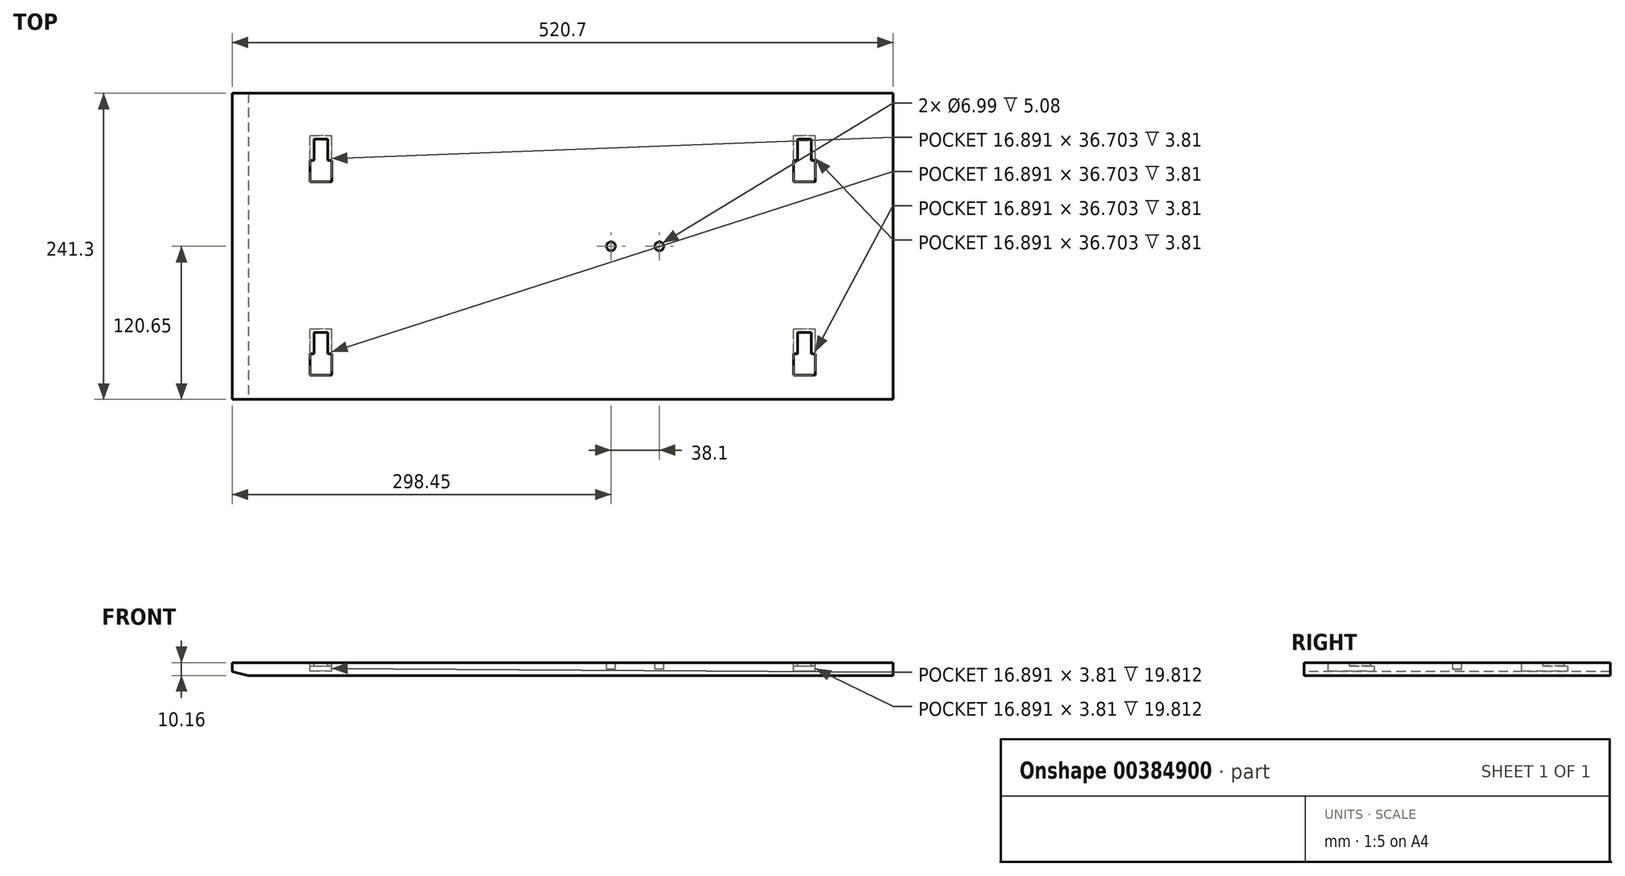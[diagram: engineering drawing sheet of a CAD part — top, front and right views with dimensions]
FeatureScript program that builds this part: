
annotation { "Feature Type Name" : "Feature", "Feature Type Description" : "" }
export const myFeature = defineFeature(function(context is Context, id is Id, definition is map)
    precondition{}
    {
        {
            var Q0;
            Q0=qCreatedBy(makeId("Top.planeOp"),FACE);
            var sketch = newSketch(context, id + "F0", { "sketchPlane" : qUnion([Q0])});
            skLineSegment(sketch, "E0.bottom", {"start": v(0, 0) * mm, "end": v(520.7, 0) * mm});
            skLineSegment(sketch, "E0.top", {"start": v(0, 241.3) * mm, "end": v(520.7, 241.3) * mm});
            skLineSegment(sketch, "E0.left", {"start": v(0, 0) * mm, "end": v(0, 241.3) * mm});
            skLineSegment(sketch, "E0.right", {"start": v(520.7, 0) * mm, "end": v(520.7, 241.3) * mm});
            skSolve(sketch);
        }
        {
            var Q0;
            Q0=makeQuery(id+"F0.imprint","IMPRINT",FACE,{"disambiguationData":[TD([[makeQuery(id+"F0.imprint","IMPRINT",EDGE,{"derivedFrom":sQuery(id+"F0.wireOp",EDGE,"E0.bottom")}),1.0]])]});
            extrude(context, id + "F1", {"entities" : qUnion([Q0]), "depth" : 10.16 * mm});
        }
        {
            var Q0;
            Q0=makeQuery(id+"F1.opExtrude","CAP_FACE",FACE,{"disambiguationData":[OSD([sQuery(id+"F0.wireOp",EDGE,"E0.bottom"),sQuery(id+"F0.wireOp",EDGE,"E0.top"),sQuery(id+"F0.wireOp",EDGE,"E0.left"),sQuery(id+"F0.wireOp",EDGE,"E0.right")])],"isStart":false});
            var sketch = newSketch(context, id + "F2", { "sketchPlane" : qUnion([Q0])});
            skCircle(sketch, "E1", {"center": v(336.55, 120.65) * mm, "radius": 3.5 * mm});
            skCircle(sketch, "E2", {"center": v(298.45, 120.65) * mm, "radius": 3.5 * mm});
            skSolve(sketch);
        }
        {
            var Q0;
            Q0=makeQuery(id+"F1.opExtrude","CAP_FACE",FACE,{"disambiguationData":[OSD([sQuery(id+"F0.wireOp",EDGE,"E0.bottom"),sQuery(id+"F0.wireOp",EDGE,"E0.top"),sQuery(id+"F0.wireOp",EDGE,"E0.left"),sQuery(id+"F0.wireOp",EDGE,"E0.right")])],"isStart":false});
            var sketch = newSketch(context, id + "F3", { "sketchPlane" : qUnion([Q0])});
            skLineSegment(sketch, "E3.bottom", {"start": v(61.4, 19.05) * mm, "end": v(78.3, 19.05) * mm});
            skLineSegment(sketch, "E3.top", {"start": v(61.4, 55.75) * mm, "end": v(78.3, 55.75) * mm});
            skLineSegment(sketch, "E3.left", {"start": v(61.4, 19.05) * mm, "end": v(61.4, 55.75) * mm});
            skLineSegment(sketch, "E3.right", {"start": v(78.3, 19.05) * mm, "end": v(78.3, 55.75) * mm});
            skLineSegment(sketch, "E4.0.1.0", {"start": v(61.4, 171.45) * mm, "end": v(78.3, 171.45) * mm});
            skLineSegment(sketch, "E4.0.1.1", {"start": v(78.3, 171.45) * mm, "end": v(78.3, 208.15) * mm});
            skLineSegment(sketch, "E4.0.1.2", {"start": v(61.4, 208.15) * mm, "end": v(78.3, 208.15) * mm});
            skLineSegment(sketch, "E4.0.1.3", {"start": v(61.4, 171.45) * mm, "end": v(61.4, 208.15) * mm});
            skLineSegment(sketch, "E4.1.0.0", {"start": v(442.4, 19.05) * mm, "end": v(459.3, 19.05) * mm});
            skLineSegment(sketch, "E4.1.0.1", {"start": v(459.3, 19.05) * mm, "end": v(459.3, 55.75) * mm});
            skLineSegment(sketch, "E4.1.0.2", {"start": v(442.4, 55.75) * mm, "end": v(459.3, 55.75) * mm});
            skLineSegment(sketch, "E4.1.0.3", {"start": v(442.4, 19.05) * mm, "end": v(442.4, 55.75) * mm});
            skLineSegment(sketch, "E4.1.1.0", {"start": v(442.4, 171.45) * mm, "end": v(459.3, 171.45) * mm});
            skLineSegment(sketch, "E4.1.1.1", {"start": v(459.3, 171.45) * mm, "end": v(459.3, 208.15) * mm});
            skLineSegment(sketch, "E4.1.1.2", {"start": v(442.4, 208.15) * mm, "end": v(459.3, 208.15) * mm});
            skLineSegment(sketch, "E4.1.1.3", {"start": v(442.4, 171.45) * mm, "end": v(442.4, 208.15) * mm});
            skLineSegment(sketch, "E4.direction1", {"start": v(61.4, 19.05) * mm, "end": v(442.4, 19.05) * mm, "construction": true});
            skLineSegment(sketch, "E4.direction2", {"start": v(61.4, 19.05) * mm, "end": v(61.4, 171.45) * mm, "construction": true});
            skSolve(sketch);
        }
        {
            var Q0;
            Q0=makeQuery(id+"F3.imprint","IMPRINT",FACE,{"disambiguationData":[TD([[makeQuery(id+"F3.imprint","IMPRINT",EDGE,{"derivedFrom":sQuery(id+"F3.wireOp",EDGE,"E4.0.1.0")}),1.0]])]});
            var Q1;
            Q1=makeQuery(id+"F3.imprint","IMPRINT",FACE,{"disambiguationData":[TD([[makeQuery(id+"F3.imprint","IMPRINT",EDGE,{"derivedFrom":sQuery(id+"F3.wireOp",EDGE,"E3.bottom")}),1.0]])]});
            var Q2;
            Q2=makeQuery(id+"F3.imprint","IMPRINT",FACE,{"disambiguationData":[TD([[makeQuery(id+"F3.imprint","IMPRINT",EDGE,{"derivedFrom":sQuery(id+"F3.wireOp",EDGE,"E4.1.0.0")}),1.0]])]});
            var Q3;
            Q3=makeQuery(id+"F3.imprint","IMPRINT",FACE,{"disambiguationData":[TD([[makeQuery(id+"F3.imprint","IMPRINT",EDGE,{"derivedFrom":sQuery(id+"F3.wireOp",EDGE,"E4.1.1.0")}),1.0]])]});
            extrude(context, id + "F4", {"entities" : qUnion([Q0, Q1, Q2, Q3]), "operationType" : NewBodyOperationType.REMOVE, "oppositeDirection" : true, "depth" : 6.35 * mm});
        }
        {
            var Q0;
            Q0=makeQuery(id+"F1.opExtrude","CAP_FACE",FACE,{"disambiguationData":[OSD([sQuery(id+"F0.wireOp",EDGE,"E0.bottom"),sQuery(id+"F0.wireOp",EDGE,"E0.top"),sQuery(id+"F0.wireOp",EDGE,"E0.left"),sQuery(id+"F0.wireOp",EDGE,"E0.right")])],"isStart":false});
            var sketch = newSketch(context, id + "F5", { "sketchPlane" : qUnion([Q0])});
            skLineSegment(sketch, "E5.bottom", {"start": v(61.4, 55.75) * mm, "end": v(64.39, 55.75) * mm});
            skLineSegment(sketch, "E5.top", {"start": v(61.4, 35.94) * mm, "end": v(64.39, 35.94) * mm});
            skLineSegment(sketch, "E5.left", {"start": v(61.4, 55.75) * mm, "end": v(61.4, 35.94) * mm});
            skLineSegment(sketch, "E5.right", {"start": v(64.39, 55.75) * mm, "end": v(64.39, 35.94) * mm});
            skLineSegment(sketch, "E6.bottom", {"start": v(78.3, 55.75) * mm, "end": v(75.31, 55.75) * mm});
            skLineSegment(sketch, "E6.top", {"start": v(78.3, 35.94) * mm, "end": v(75.31, 35.94) * mm});
            skLineSegment(sketch, "E6.left", {"start": v(78.3, 55.75) * mm, "end": v(78.3, 35.94) * mm});
            skLineSegment(sketch, "E6.right", {"start": v(75.31, 55.75) * mm, "end": v(75.31, 35.94) * mm});
            skLineSegment(sketch, "E7.0.1.0", {"start": v(78.3, 188.34) * mm, "end": v(75.31, 188.34) * mm});
            skLineSegment(sketch, "E7.0.1.1", {"start": v(75.31, 208.15) * mm, "end": v(75.31, 188.34) * mm});
            skLineSegment(sketch, "E7.0.1.2", {"start": v(78.3, 208.15) * mm, "end": v(78.3, 188.34) * mm});
            skLineSegment(sketch, "E7.0.1.3", {"start": v(78.3, 208.15) * mm, "end": v(75.31, 208.15) * mm});
            skLineSegment(sketch, "E7.0.1.4", {"start": v(64.39, 208.15) * mm, "end": v(64.39, 188.34) * mm});
            skLineSegment(sketch, "E7.0.1.5", {"start": v(61.4, 208.15) * mm, "end": v(61.4, 188.34) * mm});
            skLineSegment(sketch, "E7.0.1.6", {"start": v(61.4, 208.15) * mm, "end": v(64.39, 208.15) * mm});
            skLineSegment(sketch, "E7.0.1.7", {"start": v(61.4, 188.34) * mm, "end": v(64.39, 188.34) * mm});
            skLineSegment(sketch, "E7.1.0.0", {"start": v(459.3, 35.94) * mm, "end": v(456.31, 35.94) * mm});
            skLineSegment(sketch, "E7.1.0.1", {"start": v(456.31, 55.75) * mm, "end": v(456.31, 35.94) * mm});
            skLineSegment(sketch, "E7.1.0.2", {"start": v(459.3, 55.75) * mm, "end": v(459.3, 35.94) * mm});
            skLineSegment(sketch, "E7.1.0.3", {"start": v(459.3, 55.75) * mm, "end": v(456.31, 55.75) * mm});
            skLineSegment(sketch, "E7.1.0.4", {"start": v(445.39, 55.75) * mm, "end": v(445.39, 35.94) * mm});
            skLineSegment(sketch, "E7.1.0.5", {"start": v(442.4, 55.75) * mm, "end": v(442.4, 35.94) * mm});
            skLineSegment(sketch, "E7.1.0.6", {"start": v(442.4, 55.75) * mm, "end": v(445.39, 55.75) * mm});
            skLineSegment(sketch, "E7.1.0.7", {"start": v(442.4, 35.94) * mm, "end": v(445.39, 35.94) * mm});
            skLineSegment(sketch, "E7.1.1.0", {"start": v(459.3, 188.34) * mm, "end": v(456.31, 188.34) * mm});
            skLineSegment(sketch, "E7.1.1.1", {"start": v(456.31, 208.15) * mm, "end": v(456.31, 188.34) * mm});
            skLineSegment(sketch, "E7.1.1.2", {"start": v(459.3, 208.15) * mm, "end": v(459.3, 188.34) * mm});
            skLineSegment(sketch, "E7.1.1.3", {"start": v(459.3, 208.15) * mm, "end": v(456.31, 208.15) * mm});
            skLineSegment(sketch, "E7.1.1.4", {"start": v(445.39, 208.15) * mm, "end": v(445.39, 188.34) * mm});
            skLineSegment(sketch, "E7.1.1.5", {"start": v(442.4, 208.15) * mm, "end": v(442.4, 188.34) * mm});
            skLineSegment(sketch, "E7.1.1.6", {"start": v(442.4, 208.15) * mm, "end": v(445.39, 208.15) * mm});
            skLineSegment(sketch, "E7.1.1.7", {"start": v(442.4, 188.34) * mm, "end": v(445.39, 188.34) * mm});
            skLineSegment(sketch, "E7.direction1", {"start": v(75.31, 35.94) * mm, "end": v(456.31, 35.94) * mm, "construction": true});
            skLineSegment(sketch, "E7.direction2", {"start": v(75.31, 35.94) * mm, "end": v(75.31, 188.34) * mm, "construction": true});
            skLineSegment(sketch, "E8.bottom", {"start": v(64.39, 55.75) * mm, "end": v(75.31, 55.75) * mm});
            skLineSegment(sketch, "E8.top", {"start": v(64.39, 52.58) * mm, "end": v(75.31, 52.58) * mm});
            skLineSegment(sketch, "E8.left", {"start": v(64.39, 55.75) * mm, "end": v(64.39, 52.58) * mm});
            skLineSegment(sketch, "E8.right", {"start": v(75.31, 55.75) * mm, "end": v(75.31, 52.58) * mm});
            skSolve(sketch);
        }
        {
            var Q0;
            Q0=makeQuery(id+"F5.imprint","IMPRINT",FACE,{"disambiguationData":[TD([[makeQuery(id+"F5.imprint","IMPRINT",EDGE,{"derivedFrom":sQuery(id+"F5.wireOp",EDGE,"E7.0.1.4")}),-1.0]])]});
            var Q1;
            Q1=makeQuery(id+"F5.imprint","IMPRINT",FACE,{"disambiguationData":[TD([[makeQuery(id+"F5.imprint","IMPRINT",EDGE,{"derivedFrom":sQuery(id+"F5.wireOp",EDGE,"E7.0.1.0")}),-1.0]])]});
            var Q2;
            Q2=makeQuery(id+"F5.imprint","IMPRINT",FACE,{"disambiguationData":[TD([[makeQuery(id+"F5.imprint","IMPRINT",EDGE,{"derivedFrom":sQuery(id+"F5.wireOp",EDGE,"E5.bottom")}),-1.0]])]});
            var Q3;
            Q3=makeQuery(id+"F5.imprint","IMPRINT",FACE,{"disambiguationData":[TD([[makeQuery(id+"F5.imprint","IMPRINT",EDGE,{"derivedFrom":sQuery(id+"F5.wireOp",EDGE,"E6.bottom")}),-1.0]])]});
            var Q4;
            Q4=makeQuery(id+"F5.imprint","IMPRINT",FACE,{"disambiguationData":[TD([[makeQuery(id+"F5.imprint","IMPRINT",EDGE,{"derivedFrom":sQuery(id+"F5.wireOp",EDGE,"E7.1.0.0")}),-1.0]])]});
            var Q5;
            Q5=makeQuery(id+"F5.imprint","IMPRINT",FACE,{"disambiguationData":[TD([[makeQuery(id+"F5.imprint","IMPRINT",EDGE,{"derivedFrom":sQuery(id+"F5.wireOp",EDGE,"E7.1.0.4")}),-1.0]])]});
            var Q6;
            Q6=makeQuery(id+"F5.imprint","IMPRINT",FACE,{"disambiguationData":[TD([[makeQuery(id+"F5.imprint","IMPRINT",EDGE,{"derivedFrom":sQuery(id+"F5.wireOp",EDGE,"E7.1.1.4")}),-1.0]])]});
            var Q7;
            Q7=makeQuery(id+"F5.imprint","IMPRINT",FACE,{"disambiguationData":[TD([[makeQuery(id+"F5.imprint","IMPRINT",EDGE,{"derivedFrom":sQuery(id+"F5.wireOp",EDGE,"E7.1.1.0")}),-1.0]])]});
            extrude(context, id + "F6", {"entities" : qUnion([Q0, Q1, Q2, Q3, Q4, Q5, Q6, Q7]), "operationType" : NewBodyOperationType.ADD, "oppositeDirection" : true, "depth" : 2.54 * mm});
        }
        {
            var Q0;
            Q0=makeQuery(id+"F6.boolean.opBoolean","MERGE",FACE,{"derivedFrom":[makeQuery(id+"F1.opExtrude","CAP_FACE",FACE,{"disambiguationData":[OSD([sQuery(id+"F0.wireOp",EDGE,"E0.bottom"),sQuery(id+"F0.wireOp",EDGE,"E0.top"),sQuery(id+"F0.wireOp",EDGE,"E0.left"),sQuery(id+"F0.wireOp",EDGE,"E0.right")])],"isStart":false}),makeQuery(id+"F6.opExtrude","CAP_FACE",FACE,{"disambiguationData":[OSD([sQuery(id+"F5.wireOp",EDGE,"E5.bottom"),sQuery(id+"F5.wireOp",EDGE,"E5.top"),sQuery(id+"F5.wireOp",EDGE,"E5.left"),sQuery(id+"F5.wireOp",EDGE,"E5.right"),sQuery(id+"F5.wireOp",EDGE,"E8.left")])],"isStart":true}),makeQuery(id+"F6.opExtrude","CAP_FACE",FACE,{"disambiguationData":[OSD([sQuery(id+"F5.wireOp",EDGE,"E6.bottom"),sQuery(id+"F5.wireOp",EDGE,"E6.top"),sQuery(id+"F5.wireOp",EDGE,"E6.left"),sQuery(id+"F5.wireOp",EDGE,"E6.right"),sQuery(id+"F5.wireOp",EDGE,"E8.right")])],"isStart":true}),makeQuery(id+"F6.opExtrude","CAP_FACE",FACE,{"disambiguationData":[OSD([sQuery(id+"F5.wireOp",EDGE,"E7.0.1.0"),sQuery(id+"F5.wireOp",EDGE,"E7.0.1.1"),sQuery(id+"F5.wireOp",EDGE,"E7.0.1.2"),sQuery(id+"F5.wireOp",EDGE,"E7.0.1.3")])],"isStart":true}),makeQuery(id+"F6.opExtrude","CAP_FACE",FACE,{"disambiguationData":[OSD([sQuery(id+"F5.wireOp",EDGE,"E7.0.1.4"),sQuery(id+"F5.wireOp",EDGE,"E7.0.1.5"),sQuery(id+"F5.wireOp",EDGE,"E7.0.1.6"),sQuery(id+"F5.wireOp",EDGE,"E7.0.1.7")])],"isStart":true}),makeQuery(id+"F6.opExtrude","CAP_FACE",FACE,{"disambiguationData":[OSD([sQuery(id+"F5.wireOp",EDGE,"E7.1.0.0"),sQuery(id+"F5.wireOp",EDGE,"E7.1.0.1"),sQuery(id+"F5.wireOp",EDGE,"E7.1.0.2"),sQuery(id+"F5.wireOp",EDGE,"E7.1.0.3")])],"isStart":true}),makeQuery(id+"F6.opExtrude","CAP_FACE",FACE,{"disambiguationData":[OSD([sQuery(id+"F5.wireOp",EDGE,"E7.1.0.4"),sQuery(id+"F5.wireOp",EDGE,"E7.1.0.5"),sQuery(id+"F5.wireOp",EDGE,"E7.1.0.6"),sQuery(id+"F5.wireOp",EDGE,"E7.1.0.7")])],"isStart":true}),makeQuery(id+"F6.opExtrude","CAP_FACE",FACE,{"disambiguationData":[OSD([sQuery(id+"F5.wireOp",EDGE,"E7.1.1.0"),sQuery(id+"F5.wireOp",EDGE,"E7.1.1.1"),sQuery(id+"F5.wireOp",EDGE,"E7.1.1.2"),sQuery(id+"F5.wireOp",EDGE,"E7.1.1.3")])],"isStart":true}),makeQuery(id+"F6.opExtrude","CAP_FACE",FACE,{"disambiguationData":[OSD([sQuery(id+"F5.wireOp",EDGE,"E7.1.1.4"),sQuery(id+"F5.wireOp",EDGE,"E7.1.1.5"),sQuery(id+"F5.wireOp",EDGE,"E7.1.1.6"),sQuery(id+"F5.wireOp",EDGE,"E7.1.1.7")])],"isStart":true})]});
            var sketch = newSketch(context, id + "F7", { "sketchPlane" : qUnion([Q0])});
            skLineSegment(sketch, "E9.bottom", {"start": v(64.39, 55.75) * mm, "end": v(75.31, 55.75) * mm});
            skLineSegment(sketch, "E9.top", {"start": v(64.39, 52.77) * mm, "end": v(75.31, 52.77) * mm});
            skLineSegment(sketch, "E9.left", {"start": v(64.39, 55.75) * mm, "end": v(64.39, 52.77) * mm});
            skLineSegment(sketch, "E9.right", {"start": v(75.31, 55.75) * mm, "end": v(75.31, 52.77) * mm});
            skLineSegment(sketch, "E10.0.1.0", {"start": v(64.39, 205.17) * mm, "end": v(75.31, 205.17) * mm});
            skLineSegment(sketch, "E10.0.1.1", {"start": v(64.39, 208.15) * mm, "end": v(64.39, 205.17) * mm});
            skLineSegment(sketch, "E10.0.1.2", {"start": v(64.39, 208.15) * mm, "end": v(75.31, 208.15) * mm});
            skLineSegment(sketch, "E10.0.1.3", {"start": v(75.31, 208.15) * mm, "end": v(75.31, 205.17) * mm});
            skLineSegment(sketch, "E10.1.0.0", {"start": v(445.39, 52.77) * mm, "end": v(456.31, 52.77) * mm});
            skLineSegment(sketch, "E10.1.0.1", {"start": v(445.39, 55.75) * mm, "end": v(445.39, 52.77) * mm});
            skLineSegment(sketch, "E10.1.0.2", {"start": v(445.39, 55.75) * mm, "end": v(456.31, 55.75) * mm});
            skLineSegment(sketch, "E10.1.0.3", {"start": v(456.31, 55.75) * mm, "end": v(456.31, 52.77) * mm});
            skLineSegment(sketch, "E10.1.1.0", {"start": v(445.39, 205.17) * mm, "end": v(456.31, 205.17) * mm});
            skLineSegment(sketch, "E10.1.1.1", {"start": v(445.39, 208.15) * mm, "end": v(445.39, 205.17) * mm});
            skLineSegment(sketch, "E10.1.1.2", {"start": v(445.39, 208.15) * mm, "end": v(456.31, 208.15) * mm});
            skLineSegment(sketch, "E10.1.1.3", {"start": v(456.31, 208.15) * mm, "end": v(456.31, 205.17) * mm});
            skLineSegment(sketch, "E10.direction1", {"start": v(64.39, 52.77) * mm, "end": v(445.39, 52.77) * mm, "construction": true});
            skLineSegment(sketch, "E10.direction2", {"start": v(64.39, 52.77) * mm, "end": v(64.39, 205.17) * mm, "construction": true});
            skSolve(sketch);
        }
        {
            var Q0;
            Q0=makeQuery(id+"F7.imprint","IMPRINT",FACE,{"disambiguationData":[TD([[makeQuery(id+"F7.imprint","IMPRINT",EDGE,{"derivedFrom":sQuery(id+"F7.wireOp",EDGE,"E9.bottom")}),-1.0]])]});
            var Q1;
            Q1=makeQuery(id+"F7.imprint","IMPRINT",FACE,{"disambiguationData":[TD([[makeQuery(id+"F7.imprint","IMPRINT",EDGE,{"derivedFrom":sQuery(id+"F7.wireOp",EDGE,"E10.0.1.0")}),1.0]])]});
            var Q2;
            Q2=makeQuery(id+"F7.imprint","IMPRINT",FACE,{"disambiguationData":[TD([[makeQuery(id+"F7.imprint","IMPRINT",EDGE,{"derivedFrom":sQuery(id+"F7.wireOp",EDGE,"E10.1.0.0")}),1.0]])]});
            var Q3;
            Q3=makeQuery(id+"F7.imprint","IMPRINT",FACE,{"disambiguationData":[TD([[makeQuery(id+"F7.imprint","IMPRINT",EDGE,{"derivedFrom":sQuery(id+"F7.wireOp",EDGE,"E10.1.1.0")}),1.0]])]});
            extrude(context, id + "F8", {"entities" : qUnion([Q0, Q1, Q2, Q3]), "operationType" : NewBodyOperationType.ADD, "oppositeDirection" : true, "depth" : 2.54 * mm});
        }
        {
            var Q0;
            Q0=makeQuery(id+"F2.imprint","IMPRINT",FACE,{"disambiguationData":[TD([[makeQuery(id+"F2.imprint","IMPRINT",EDGE,{"derivedFrom":sQuery(id+"F2.wireOp",EDGE,"E2")}),1.0]])]});
            var Q1;
            Q1=makeQuery(id+"F2.imprint","IMPRINT",FACE,{"disambiguationData":[TD([[makeQuery(id+"F2.imprint","IMPRINT",EDGE,{"derivedFrom":sQuery(id+"F2.wireOp",EDGE,"E1")}),1.0]])]});
            extrude(context, id + "F9", {"entities" : qUnion([Q0, Q1]), "operationType" : NewBodyOperationType.REMOVE, "oppositeDirection" : true, "depth" : 5.08 * mm});
        }
        {
            var Q0;
            Q0=makeQuery(id+"F1.opExtrude","SWEPT_FACE",FACE,{"disambiguationData":[OSD([sQuery(id+"F0.wireOp",EDGE,"E0.bottom")])]});
            var sketch = newSketch(context, id + "F10", { "sketchPlane" : qUnion([Q0])});
            skLineSegment(sketch, "E11", {"start": v(0, 3.17) * mm, "end": v(12.7, 0) * mm});
            skLineSegment(sketch, "E12", {"start": v(0, 3.17) * mm, "end": v(0, 0) * mm});
            skLineSegment(sketch, "E13", {"start": v(0, 0) * mm, "end": v(12.7, 0) * mm});
            skSolve(sketch);
        }
        {
            var Q0;
            Q0=makeQuery(id+"F10.imprint","IMPRINT",FACE,{"disambiguationData":[TD([[makeQuery(id+"F10.imprint","IMPRINT",EDGE,{"derivedFrom":sQuery(id+"F10.wireOp",EDGE,"E11")}),-1.0]])]});
            extrude(context, id + "F11", {"entities" : qUnion([Q0]), "operationType" : NewBodyOperationType.REMOVE, "oppositeDirection" : true, "depth" : 254 * mm});
        }
    });
